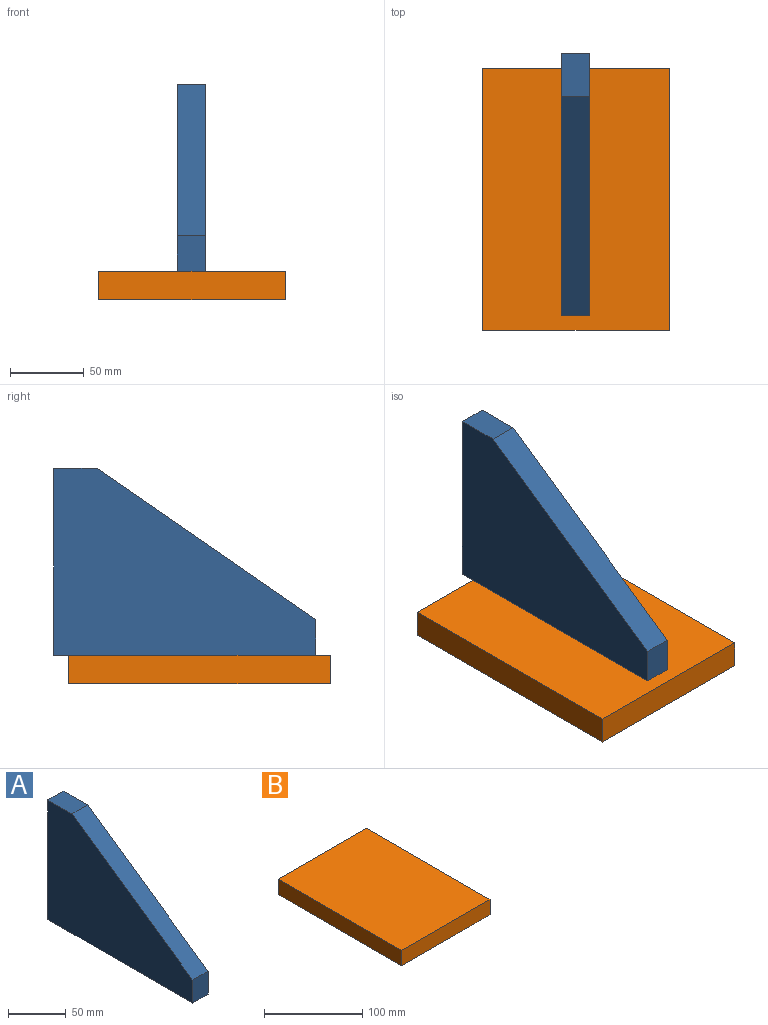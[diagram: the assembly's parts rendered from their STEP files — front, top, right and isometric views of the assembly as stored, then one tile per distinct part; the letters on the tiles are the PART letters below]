
ASSEMBLY  parts=2 mates=1
PART A: 7 faces, bbox 19.1x177.8x127 mm
  f0: plane 29.5x19.05mm, normal (0,0,1), area 562mm2, adj f1,f4,f5,f6
  f1: plane 177.8x127mm, normal (1,0,0), area 14975.5mm2, adj f0,f2,f3,f4,f6
  f2: plane 24.44x19.05mm, normal (0,-1,0), area 465.5mm2, adj f1,f3,f5,f6
  f3: plane 177.8x19.05mm, normal (0,0,-1), area 3387.1mm2, adj f1,f2,f4,f5
  f4: plane 127x19.05mm, normal (0,1,0), area 2419.3mm2, adj f0,f1,f3,f5
  f5: plane 177.8x127mm, normal (-1,0,0), area 14975.5mm2, adj f0,f2,f3,f4,f6
  f6: plane 148.3x102.56mm, normal (0,-0.57,0.82), area 3434.9mm2, adj f0,f1,f2,f5
PART B: 6 faces, bbox 127x177.8x19.1 mm
  f0: plane 127x19.05mm, normal (0,1,0), area 2419.3mm2, adj f1,f3,f4,f5
  f1: plane 177.8x19.05mm, normal (-1,0,0), area 3387.1mm2, adj f0,f2,f4,f5
  f2: plane 127x19.05mm, normal (0,-1,0), area 2419.3mm2, adj f1,f3,f4,f5
  f3: plane 177.8x19.05mm, normal (1,0,0), area 3387.1mm2, adj f0,f2,f4,f5
  f4: plane 177.8x127mm, normal (0,0,1), area 22580.6mm2, adj f0,f1,f2,f3
  f5: plane 177.8x127mm, normal (0,0,-1), area 22580.6mm2, adj f0,f1,f2,f3
PLACE A t=(116.76,-10.06,-48.66)mm
PLACE B t=(63.39,-43.08,-28.33)mm
MATE planar A.f3 <-> B.f4  axis (0,0,-1) through (126.29,55.85,-9.28)mm
